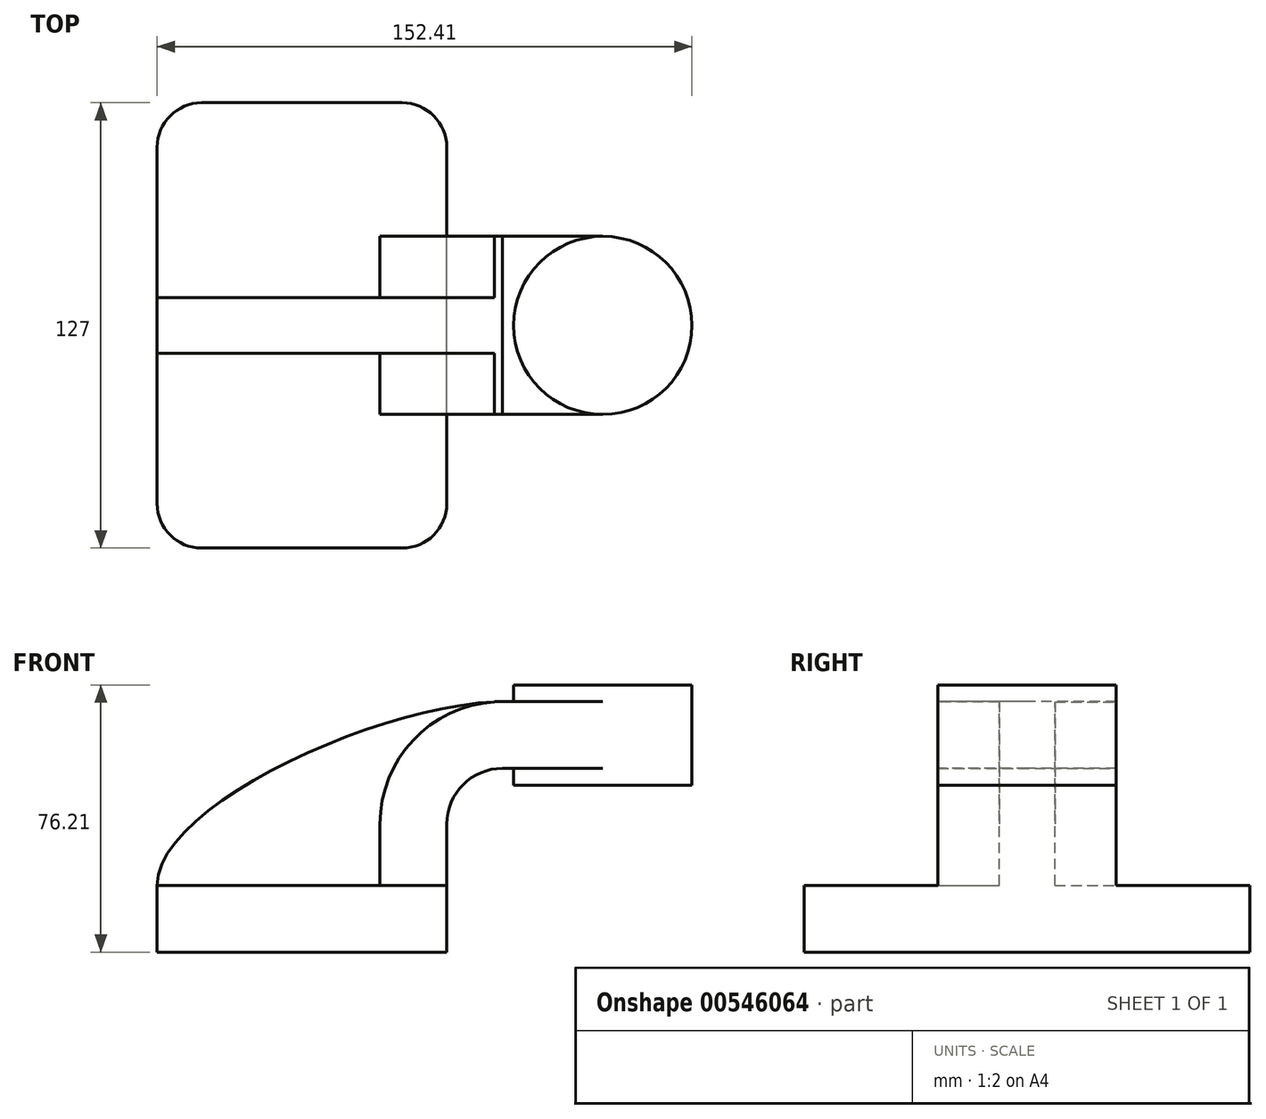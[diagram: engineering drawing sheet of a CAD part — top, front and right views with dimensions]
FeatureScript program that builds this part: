
annotation { "Feature Type Name" : "Feature", "Feature Type Description" : "" }
export const myFeature = defineFeature(function(context is Context, id is Id, definition is map)
    precondition{}
    {
        {
            var Q0;
            Q0=qCreatedBy(makeId("Front.planeOp"),FACE);
            var sketch = newSketch(context, id + "F0", { "sketchPlane" : qUnion([Q0])});
            skLineSegment(sketch, "E0.bottom", {"start": v(-41.28, -9.53) * mm, "end": v(41.28, -9.53) * mm});
            skLineSegment(sketch, "E0.top", {"start": v(-41.28, 9.52) * mm, "end": v(41.28, 9.52) * mm});
            skLineSegment(sketch, "E0.left", {"start": v(-41.28, -9.53) * mm, "end": v(-41.28, 9.53) * mm});
            skLineSegment(sketch, "E0.right", {"start": v(41.28, -9.53) * mm, "end": v(41.28, 9.53) * mm});
            skPoint(sketch, "E0.middle", {"position": v(0, 0) * mm});
            skLineSegment(sketch, "E1.bottom", {"start": v(60.33, 38.1) * mm, "end": v(111.12, 38.1) * mm});
            skLineSegment(sketch, "E1.top", {"start": v(60.33, 66.67) * mm, "end": v(111.12, 66.67) * mm});
            skLineSegment(sketch, "E1.left", {"start": v(60.33, 38.1) * mm, "end": v(60.33, 66.67) * mm});
            skLineSegment(sketch, "E1.right", {"start": v(111.12, 38.1) * mm, "end": v(111.12, 66.67) * mm});
            skPoint(sketch, "E1.middle", {"position": v(85.72, 52.39) * mm});
            skLineSegment(sketch, "E2", {"start": v(41.27, 9.53) * mm, "end": v(41.27, 27) * mm});
            skArc(sketch, "E3", {"start": v(41.27, 27) * mm, "mid": v(45.92, 38.23) * mm, "end": v(57.15, 42.88) * mm});
            skLineSegment(sketch, "E4", {"start": v(57.15, 42.88) * mm, "end": v(85.72, 42.88) * mm});
            skLineSegment(sketch, "E5.0", {"start": v(57.15, 61.93) * mm, "end": v(85.72, 61.93) * mm});
            skArc(sketch, "E5.1", {"start": v(22.23, 27) * mm, "mid": v(32.45, 51.7) * mm, "end": v(57.15, 61.93) * mm});
            skLineSegment(sketch, "E5.2", {"start": v(22.22, 9.53) * mm, "end": v(22.22, 27) * mm});
            skFitSpline(sketch, "E6", {"points": [v(-41.28, 9.53) * mm, v(57.15, 61.93) * mm], "startDerivative": vector(0.15, 69.21) * mm, "endDerivative": vector(103.35, 1.63) * mm});
            skLineSegment(sketch, "E7", {"start": v(85.72, 52.39) * mm, "end": v(85.72, 66.67) * mm});
            skLineSegment(sketch, "E8", {"start": v(85.72, 66.67) * mm, "end": v(85.72, 52.39) * mm});
            skLineSegment(sketch, "E9", {"start": v(85.72, 38.1) * mm, "end": v(85.72, 52.39) * mm});
            skSolve(sketch);
        }
        {
            var Q0;
            Q0=makeQuery(id+"F0.imprint","IMPRINT",FACE,{"disambiguationData":[TD([[makeQuery(id+"F0.imprint","IMPRINT",EDGE,{"derivedFrom":sQuery(id+"F0.wireOp",EDGE,"E0.bottom")}),1.0]])]});
            extrude(context, id + "F1", {"entities" : qUnion([Q0]), "endBound" : BoundingType.SYMMETRIC, "depth" : 127 * mm, "offsetDistance" : 25.4 * mm});
        }
        {
            var Q0;
            {var subQ0=sQuery(id+"F0.wireOp",EDGE,"E4");var subQ1=sQuery(id+"F0.wireOp",EDGE,"E1.left");var subQ2=makeQuery(id+"F0.imprint","INTERSECT",VERTEX,{"derivedFrom":[subQ1,subQ0]});Q0=makeQuery(id+"F0.imprint","IMPRINT",FACE,{"disambiguationData":[TD([[makeQuery(id+"F0.imprint","IMPRINT",EDGE,{"disambiguationData":[TD([[subQ2,-1.0]])],"derivedFrom":subQ1}),-1.0]])]});}
            var Q1;
            {var subQ1=sQuery(id+"F0.wireOp",EDGE,"E2");Q1=makeQuery(id+"F0.imprint","IMPRINT",FACE,{"disambiguationData":[TD([[makeQuery(id+"F0.imprint","IMPRINT",EDGE,{"derivedFrom":subQ1}),1.0]])]});}
            extrude(context, id + "F2", {"entities" : qUnion([Q0, Q1]), "operationType" : NewBodyOperationType.ADD, "endBound" : BoundingType.SYMMETRIC, "depth" : 50.8 * mm, "offsetDistance" : 25.4 * mm});
        }
        {
            var Q0;
            {var subQ3=sQuery(id+"F0.wireOp",EDGE,"E5.2");Q0=makeQuery(id+"F0.imprint","IMPRINT",FACE,{"disambiguationData":[TD([[makeQuery(id+"F0.imprint","IMPRINT",EDGE,{"derivedFrom":subQ3}),1.0]])]});}
            extrude(context, id + "F3", {"entities" : qUnion([Q0]), "operationType" : NewBodyOperationType.ADD, "endBound" : BoundingType.SYMMETRIC, "depth" : 15.88 * mm, "offsetDistance" : 25.4 * mm});
        }
        {
            var Q0;
            {var subQ4=sQuery(id+"F0.wireOp",EDGE,"E1.right");Q0=makeQuery(id+"F0.imprint","IMPRINT",FACE,{"disambiguationData":[TD([[makeQuery(id+"F0.imprint","IMPRINT",EDGE,{"derivedFrom":subQ4}),1.0]])]});}
            var Q1;
            Q1=sQuery(id+"F0.wireOp",EDGE,"E9");
            revolve(context, id + "F4", {"operationType" : NewBodyOperationType.ADD, "entities" : qUnion([Q0]), "axis" : qUnion([Q1]), "revolveType" : RevolveType.FULL});
        }
        {
            var Q0;
            Q0=makeQuery(id+"F1.opExtrude","CAP_EDGE",EDGE,{"disambiguationData":[OSD([sQuery(id+"F0.wireOp",EDGE,"E0.right")])],"isStart":false});
            var Q1;
            Q1=makeQuery(id+"F1.opExtrude","CAP_EDGE",EDGE,{"disambiguationData":[OSD([sQuery(id+"F0.wireOp",EDGE,"E0.left")])],"isStart":false});
            var Q2;
            Q2=makeQuery(id+"F1.opExtrude","CAP_EDGE",EDGE,{"disambiguationData":[OSD([sQuery(id+"F0.wireOp",EDGE,"E0.right")])],"isStart":true});
            var Q3;
            Q3=makeQuery(id+"F1.opExtrude","CAP_EDGE",EDGE,{"disambiguationData":[OSD([sQuery(id+"F0.wireOp",EDGE,"E0.left")])],"isStart":true});
            fillet(context, id + "F5", {"entities" : qUnion([Q0, Q1, Q2, Q3]), "radius" : 12.7 * mm, "tangentPropagation" : true, "allowEdgeOverflow" : false});
        }
    });
